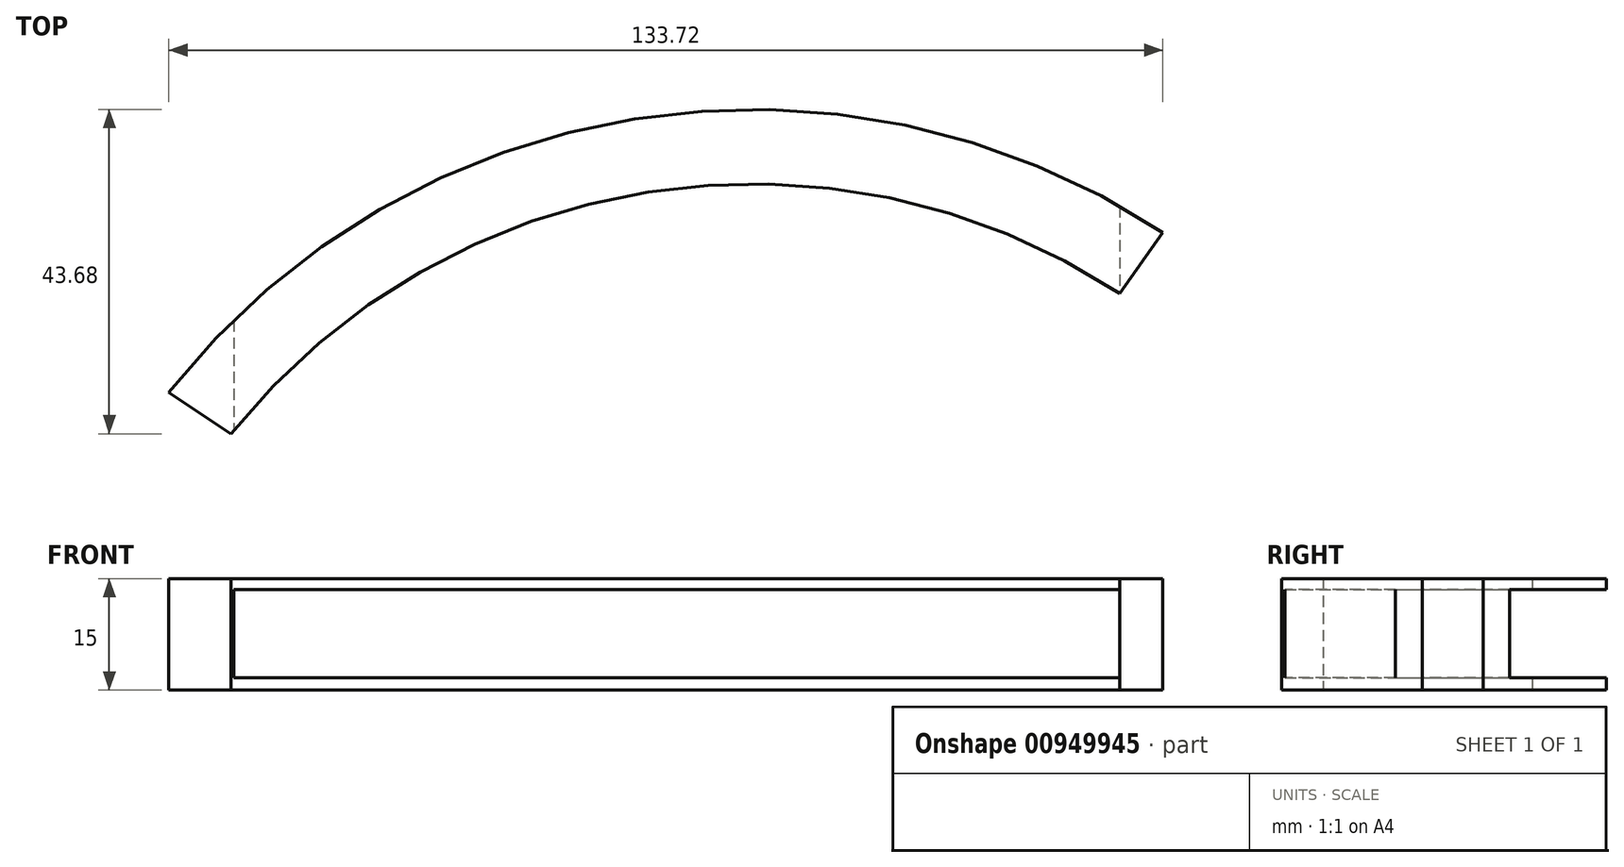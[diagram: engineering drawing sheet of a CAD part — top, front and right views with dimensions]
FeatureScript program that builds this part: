
annotation { "Feature Type Name" : "Feature", "Feature Type Description" : "" }
export const myFeature = defineFeature(function(context is Context, id is Id, definition is map)
    precondition{}
    {
        {
            var Q0;
            Q0=qCreatedBy(makeId("Top.planeOp"),FACE);
            var sketch = newSketch(context, id + "F0", { "sketchPlane" : qUnion([Q0])});
            skCircle(sketch, "E0", {"center": v(0, 0) * mm, "radius": 90 * mm});
            skCircle(sketch, "E1", {"center": v(0, 0) * mm, "radius": 100 * mm});
            skLineSegment(sketch, "E2", {"start": v(-78.56, 61.88) * mm, "end": v(-70.2, 56.32) * mm});
            skLineSegment(sketch, "E3", {"start": v(49.37, 75.25) * mm, "end": v(55.16, 83.4) * mm});
            skSolve(sketch);
        }
        {
            var Q0;
            {var subQ0=sQuery(id+"F0.wireOp",EDGE,"E2");Q0=makeQuery(id+"F0.imprint","IMPRINT",FACE,{"disambiguationData":[TD([[makeQuery(id+"F0.imprint","IMPRINT",EDGE,{"derivedFrom":subQ0}),1.0]])]});}
            extrude(context, id + "F1", {"entities" : qUnion([Q0]), "depth" : 15 * mm, "offsetDistance" : 25 * mm});
        }
        {
            var Q0;
            Q0=qCreatedBy(makeId("Front.planeOp"),FACE);
            var sketch = newSketch(context, id + "F2", { "sketchPlane" : qUnion([Q0])});
            skLineSegment(sketch, "E4.bottom", {"start": v(-69.83, 1.66) * mm, "end": v(49.35, 1.66) * mm});
            skLineSegment(sketch, "E4.top", {"start": v(-69.83, 13.56) * mm, "end": v(49.35, 13.56) * mm});
            skLineSegment(sketch, "E4.left", {"start": v(-69.83, 1.66) * mm, "end": v(-69.83, 13.56) * mm});
            skLineSegment(sketch, "E4.right", {"start": v(49.35, 1.66) * mm, "end": v(49.35, 13.56) * mm});
            skSolve(sketch);
        }
        {
            var Q0;
            Q0=makeQuery(id+"F2.imprint","IMPRINT",FACE,{"disambiguationData":[TD([[makeQuery(id+"F2.imprint","IMPRINT",EDGE,{"derivedFrom":sQuery(id+"F2.wireOp",EDGE,"E4.bottom")}),1.0]])]});
            extrude(context, id + "F3", {"entities" : qUnion([Q0]), "operationType" : NewBodyOperationType.REMOVE, "endBound" : BoundingType.THROUGH_ALL, "oppositeDirection" : true, "depth" : 25 * mm, "offsetDistance" : 25 * mm});
        }
    });
